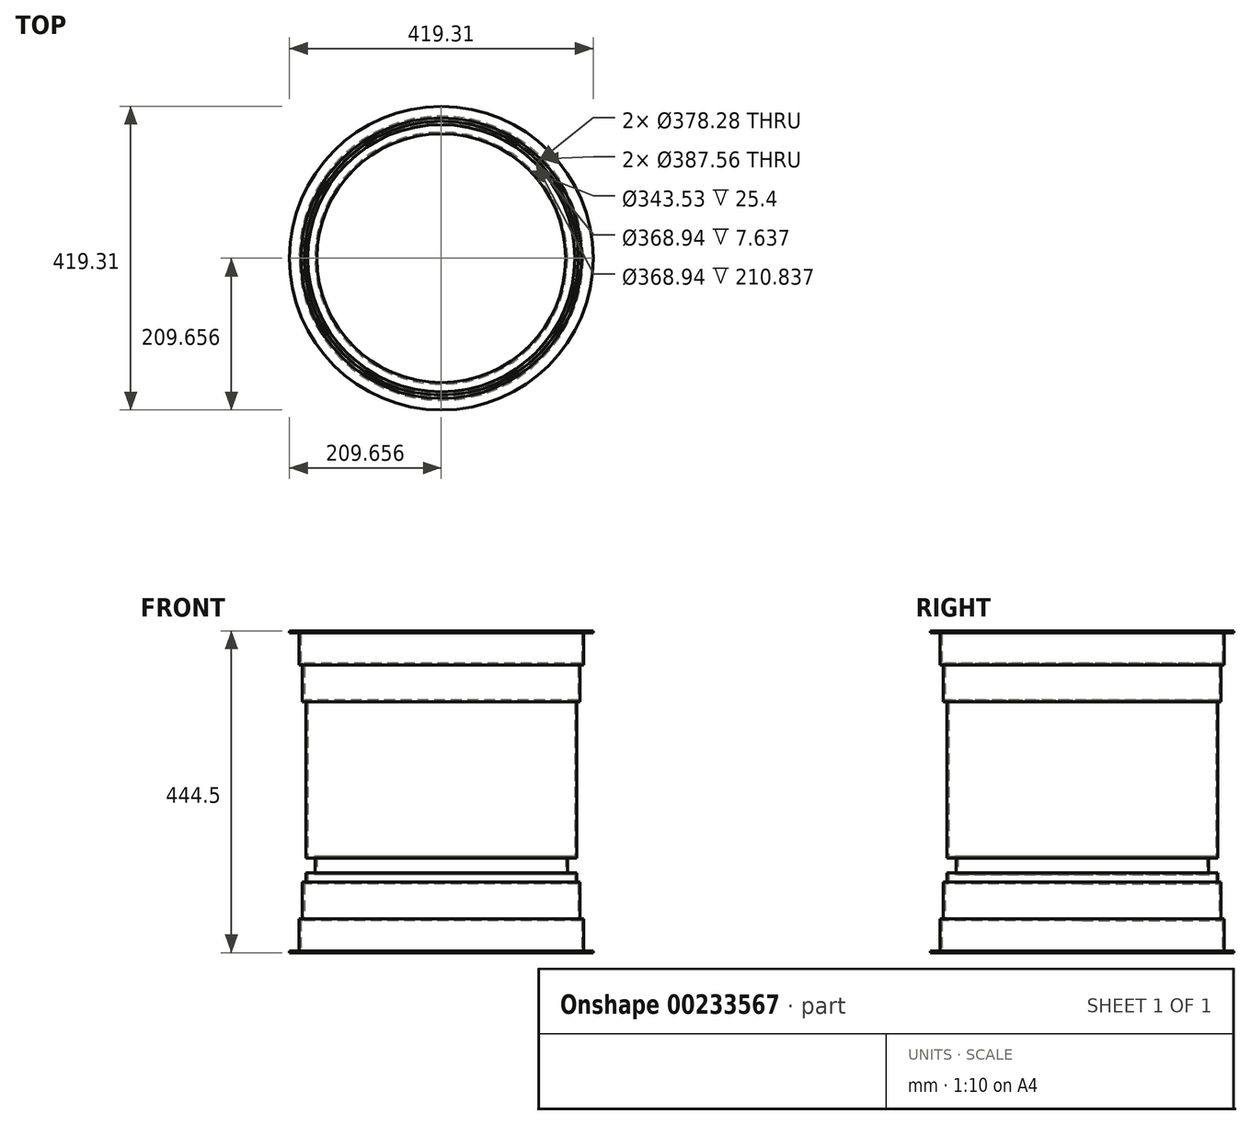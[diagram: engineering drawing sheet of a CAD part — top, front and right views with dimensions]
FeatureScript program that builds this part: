
annotation { "Feature Type Name" : "Feature", "Feature Type Description" : "" }
export const myFeature = defineFeature(function(context is Context, id is Id, definition is map)
    precondition{}
    {
        {
            var Q0;
            Q0=qCreatedBy(makeId("Top.planeOp"),FACE);
            var sketch = newSketch(context, id + "F0", { "sketchPlane" : qUnion([Q0])});
            skCircle(sketch, "E0", {"center": v(-48.75, -41.92) * mm, "radius": 184.47 * mm});
            skCircle(sketch, "E1.0", {"center": v(-48.75, -41.92) * mm, "radius": 171.77 * mm});
            skCircle(sketch, "E2", {"center": v(-48.75, -41.92) * mm, "radius": 189.14 * mm});
            skCircle(sketch, "E3", {"center": v(-48.75, -41.92) * mm, "radius": 193.78 * mm});
            skCircle(sketch, "E4.0", {"center": v(-48.75, -41.92) * mm, "radius": 206.48 * mm});
            skCircle(sketch, "E5.0", {"center": v(-48.75, -41.92) * mm, "radius": 209.65 * mm});
            skSolve(sketch);
        }
        {
            var Q0;
            Q0=makeQuery(id+"F0.imprint","IMPRINT",FACE,{"disambiguationData":[TD([[makeQuery(id+"F0.imprint","IMPRINT",EDGE,{"derivedFrom":sQuery(id+"F0.wireOp",EDGE,"E1.0")}),1.0]])]});
            extrude(context, id + "F1", {"entities" : qUnion([Q0]), "endBound" : BoundingType.SYMMETRIC, "depth" : 6.35 * mm});
        }
        {
            var Q0;
            Q0=makeQuery(id+"F0.imprint","IMPRINT",FACE,{"disambiguationData":[TD([[makeQuery(id+"F0.imprint","IMPRINT",EDGE,{"derivedFrom":sQuery(id+"F0.wireOp",EDGE,"E0")}),1.0]])]});
            extrude(context, id + "F2", {"entities" : qUnion([Q0]), "operationType" : NewBodyOperationType.ADD, "endBound" : BoundingType.SYMMETRIC, "depth" : 25.4 * mm});
        }
        {
            var Q0;
            Q0=makeQuery(id+"F0.imprint","IMPRINT",FACE,{"disambiguationData":[TD([[makeQuery(id+"F0.imprint","IMPRINT",EDGE,{"derivedFrom":sQuery(id+"F0.wireOp",EDGE,"E4.0")}),-1.0]])]});
            extrude(context, id + "F3", {"entities" : qUnion([Q0]), "endBound" : BoundingType.SYMMETRIC, "depth" : 279.4 * mm});
        }
        {
            var Q0;
            Q0=makeQuery(id+"F0.imprint","IMPRINT",FACE,{"disambiguationData":[TD([[makeQuery(id+"F0.imprint","IMPRINT",EDGE,{"derivedFrom":sQuery(id+"F0.wireOp",EDGE,"E3")}),-1.0]])]});
            extrude(context, id + "F4", {"entities" : qUnion([Q0]), "operationType" : NewBodyOperationType.ADD, "endBound" : BoundingType.SYMMETRIC, "depth" : 444.5 * mm});
        }
        {
            var Q0;
            Q0=makeQuery(id+"F0.imprint","IMPRINT",FACE,{"disambiguationData":[TD([[makeQuery(id+"F0.imprint","IMPRINT",EDGE,{"derivedFrom":sQuery(id+"F0.wireOp",EDGE,"E2")}),-1.0]])]});
            extrude(context, id + "F5", {"entities" : qUnion([Q0]), "operationType" : NewBodyOperationType.ADD, "endBound" : BoundingType.SYMMETRIC, "depth" : 355.6 * mm});
        }
        {
            var Q0;
            Q0=makeQuery(id+"F0.imprint","IMPRINT",FACE,{"disambiguationData":[TD([[makeQuery(id+"F0.imprint","IMPRINT",EDGE,{"derivedFrom":sQuery(id+"F0.wireOp",EDGE,"E0")}),-1.0]])]});
            extrude(context, id + "F6", {"entities" : qUnion([Q0]), "operationType" : NewBodyOperationType.ADD, "endBound" : BoundingType.SYMMETRIC, "depth" : 254 * mm});
        }
        {
            var Q0;
            Q0=makeQuery(id+"F1.opExtrude","CAP_FACE",FACE,{"disambiguationData":[OSD([sQuery(id+"F0.wireOp",EDGE,"E1.0")])],"isStart":false});
            extrude(context, id + "F7", {"entities" : qUnion([Q0]), "operationType" : NewBodyOperationType.REMOVE, "endBound" : BoundingType.THROUGH_ALL, "oppositeDirection" : true, "depth" : 25.4 * mm});
        }
        {
            var Q0;
            Q0=makeQuery(id+"F2.opExtrude","CAP_FACE",FACE,{"disambiguationData":[OSD([sQuery(id+"F0.wireOp",EDGE,"E0"),sQuery(id+"F0.wireOp",EDGE,"E1.0")])],"isStart":true});
            extrude(context, id + "F8", {"entities" : qUnion([Q0]), "operationType" : NewBodyOperationType.ADD, "depth" : 101.6 * mm});
        }
        {
            var Q0;
            Q0=makeQuery(id+"F2.opExtrude","CAP_FACE",FACE,{"disambiguationData":[OSD([sQuery(id+"F0.wireOp",EDGE,"E0"),sQuery(id+"F0.wireOp",EDGE,"E1.0")])],"isStart":false});
            extrude(context, id + "F9", {"entities" : qUnion([Q0]), "operationType" : NewBodyOperationType.REMOVE, "oppositeDirection" : true, "depth" : 101.6 * mm});
        }
        {
            var Q0;
            Q0=makeQuery(id+"F3.opExtrude","CAP_FACE",FACE,{"disambiguationData":[OSD([sQuery(id+"F0.wireOp",EDGE,"E4.0"),sQuery(id+"F0.wireOp",EDGE,"E5.0")])],"isStart":false});
            var Q1;
            Q1=makeQuery(id+"F4.opExtrude","CAP_FACE",FACE,{"disambiguationData":[OSD([sQuery(id+"F0.wireOp",EDGE,"E3"),sQuery(id+"F0.wireOp",EDGE,"E4.0")])],"isStart":false});
            extrude(context, id + "F10", {"entities" : qUnion([Q0]), "operationType" : NewBodyOperationType.ADD, "endBound" : BoundingType.UP_TO_SURFACE, "endBoundEntityFace" : qUnion([Q1]), "depth" : 25.4 * mm});
        }
        {
            var Q0;
            Q0=makeQuery(id+"F3.opExtrude","CAP_FACE",FACE,{"disambiguationData":[OSD([sQuery(id+"F0.wireOp",EDGE,"E4.0"),sQuery(id+"F0.wireOp",EDGE,"E5.0")])],"isStart":true});
            var Q1;
            Q1=makeQuery(id+"F4.opExtrude","CAP_FACE",FACE,{"disambiguationData":[OSD([sQuery(id+"F0.wireOp",EDGE,"E3"),sQuery(id+"F0.wireOp",EDGE,"E4.0")])],"isStart":true});
            extrude(context, id + "F11", {"entities" : qUnion([Q0]), "operationType" : NewBodyOperationType.ADD, "endBound" : BoundingType.UP_TO_SURFACE, "endBoundEntityFace" : qUnion([Q1]), "depth" : 25.4 * mm});
        }
        {
            var Q0;
            {var subQ0=sQuery(id+"F0.wireOp",EDGE,"E5.0");Q0=makeQuery(id+"F11.boolean.opBoolean","MERGE",FACE,{"derivedFrom":[makeQuery(id+"F10.boolean.opBoolean","MERGE",FACE,{"derivedFrom":[makeQuery(id+"F3.opExtrude","SWEPT_FACE",FACE,{"disambiguationData":[OSD([subQ0])]}),makeQuery(id+"F10.opExtrude","SWEPT_FACE",FACE,{"disambiguationData":[OSD([subQ0])]})]}),makeQuery(id+"F11.opExtrude","SWEPT_FACE",FACE,{"disambiguationData":[OSD([subQ0])]})]});}
            shell(context, id + "F12", {"entities" : qUnion([Q0]), "thickness" : 2.54 * mm});
        }
        {
            var Q0;
            Q0=makeQuery(id+"F4.opExtrude","CAP_EDGE",EDGE,{"disambiguationData":[OSD([sQuery(id+"F0.wireOp",EDGE,"E3")])],"isStart":true});
            var Q1;
            Q1=makeQuery(id+"F5.opExtrude","CAP_EDGE",EDGE,{"disambiguationData":[OSD([sQuery(id+"F0.wireOp",EDGE,"E2")])],"isStart":true});
            var Q2;
            Q2=makeQuery(id+"F6.opExtrude","CAP_EDGE",EDGE,{"disambiguationData":[OSD([sQuery(id+"F0.wireOp",EDGE,"E0")])],"isStart":true});
            var Q3;
            Q3=makeQuery(id+"F6.opExtrude","CAP_EDGE",EDGE,{"disambiguationData":[OSD([sQuery(id+"F0.wireOp",EDGE,"E0")])],"isStart":false});
            var Q4;
            Q4=makeQuery(id+"F5.opExtrude","CAP_EDGE",EDGE,{"disambiguationData":[OSD([sQuery(id+"F0.wireOp",EDGE,"E2")])],"isStart":false});
            var Q5;
            Q5=makeQuery(id+"F4.opExtrude","CAP_EDGE",EDGE,{"disambiguationData":[OSD([sQuery(id+"F0.wireOp",EDGE,"E3")])],"isStart":false});
            fillet(context, id + "F13", {"entities" : qUnion([Q0, Q1, Q2, Q3, Q4, Q5]), "radius" : 5.08 * mm, "tangentPropagation" : true, "allowEdgeOverflow" : false});
        }
    });
